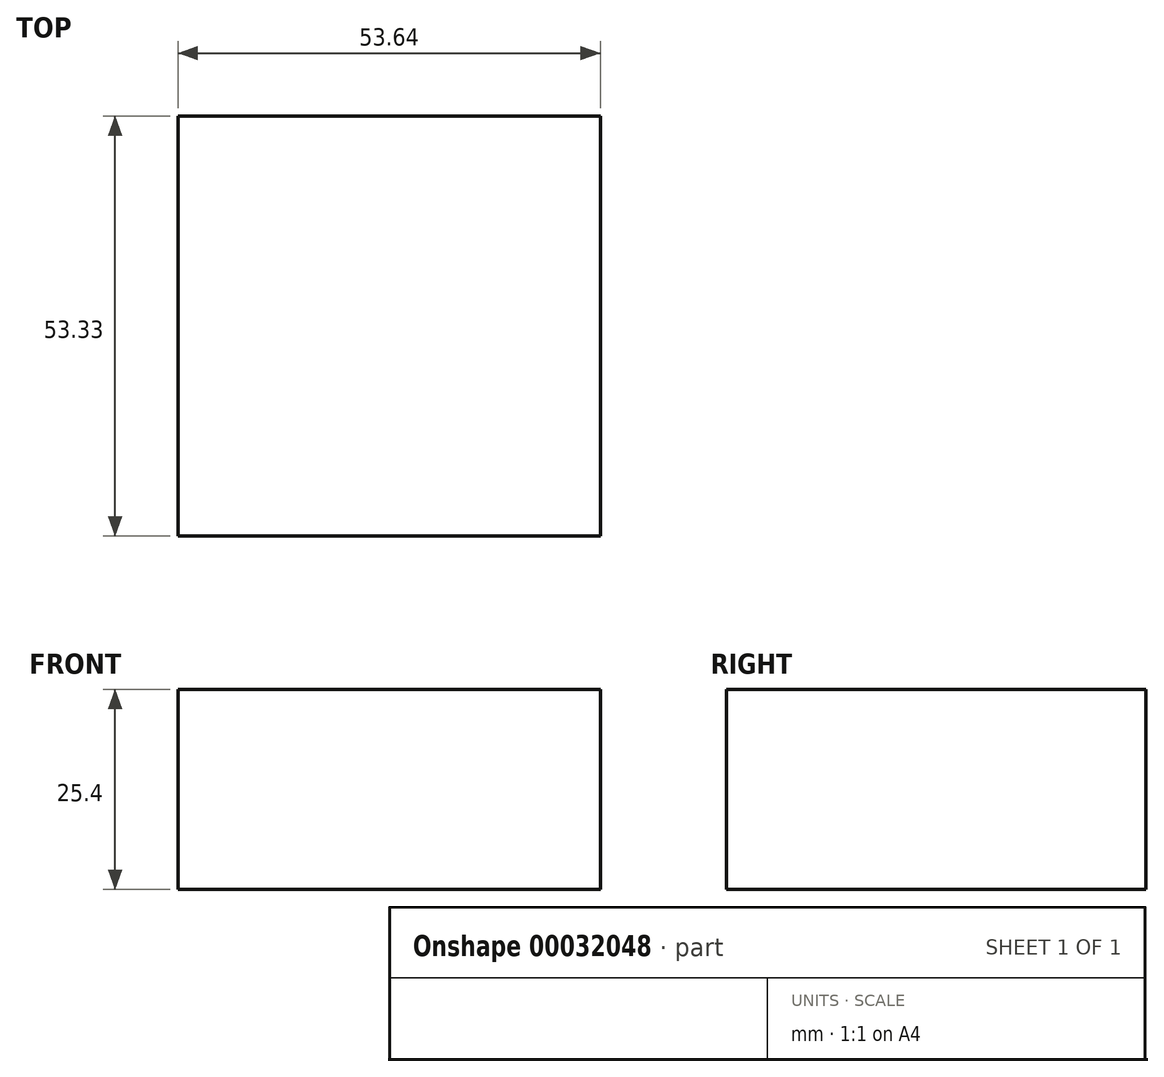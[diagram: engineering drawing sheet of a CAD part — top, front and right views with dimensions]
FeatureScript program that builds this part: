
annotation { "Feature Type Name" : "Feature", "Feature Type Description" : "" }
export const myFeature = defineFeature(function(context is Context, id is Id, definition is map)
    precondition{}
    {
        {
            var Q0;
            Q0=qCreatedBy(makeId("Top.planeOp"),FACE);
            var sketch = newSketch(context, id + "F0", { "sketchPlane" : qUnion([Q0])});
            skLineSegment(sketch, "E0.bottom", {"start": v(0, 0) * mm, "end": v(-53.64, 0) * mm});
            skLineSegment(sketch, "E0.top", {"start": v(0, -53.33) * mm, "end": v(-53.64, -53.33) * mm});
            skLineSegment(sketch, "E0.left", {"start": v(0, 0) * mm, "end": v(0, -53.33) * mm});
            skLineSegment(sketch, "E0.right", {"start": v(-53.64, 0) * mm, "end": v(-53.64, -53.33) * mm});
            skSolve(sketch);
        }
        {
            var Q0;
            Q0=makeQuery(id+"F0.imprint","IMPRINT",FACE,{"disambiguationData":[TD([[makeQuery(id+"F0.imprint","IMPRINT",EDGE,{"derivedFrom":sQuery(id+"F0.wireOp",EDGE,"E0.bottom")}),1.0]])]});
            extrude(context, id + "F1", {"entities" : qUnion([Q0]), "depth" : 25.4 * mm});
        }
    });
